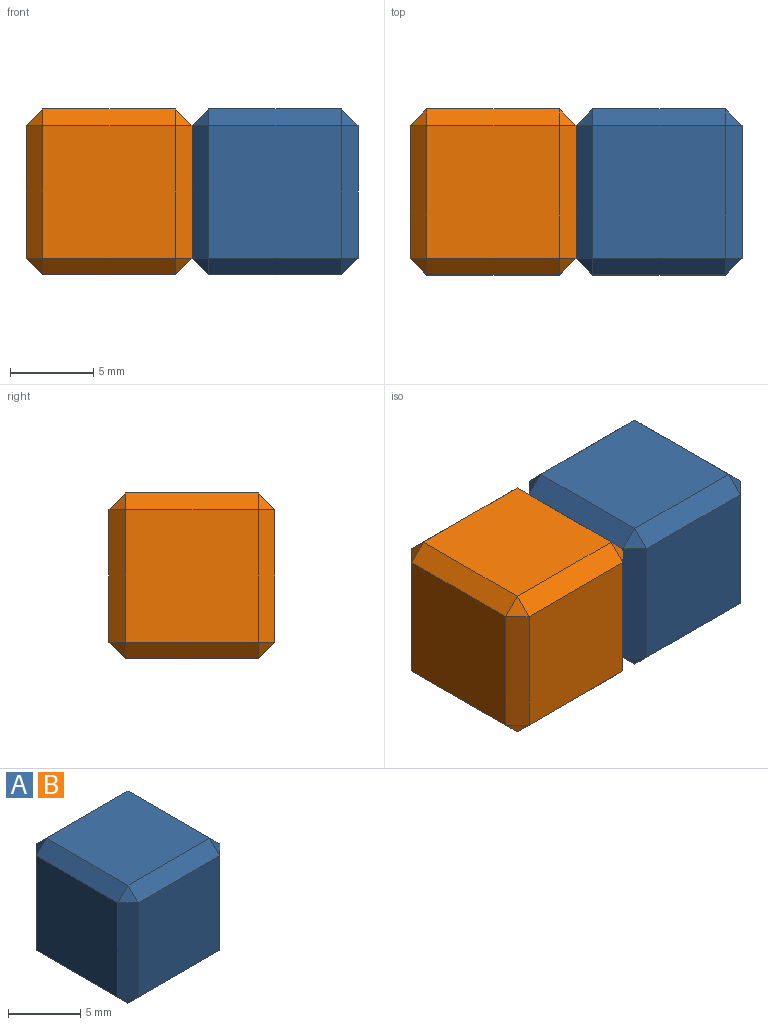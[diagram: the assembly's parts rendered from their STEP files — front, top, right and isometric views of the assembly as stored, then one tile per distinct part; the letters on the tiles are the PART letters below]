
ASSEMBLY  parts=2 mates=1
PART A: 26 faces, bbox 10x10x10 mm
  f0: plane 8x8mm, normal (1,0,0), area 64mm2, adj f11,f20,f21,f25
  f1: plane 8x8mm, normal (0,1,0), area 64mm2, adj f6,f10,f11,f12
  f2: plane 8x8mm, normal (-1,0,0), area 64mm2, adj f6,f9,f13,f14
  f3: plane 8x8mm, normal (0,-1,0), area 64mm2, adj f14,f19,f22,f25
  f4: plane 8x8mm, normal (0,0,1), area 64mm2, adj f9,f10,f19,f20
  f5: plane 8x8mm, normal (0,0,-1), area 64mm2, adj f12,f13,f21,f22
  f6: plane 8x1mm, normal (-0.71,0.71,0), area 11.3mm2, adj f1,f2,f7,f8
  f7: plane 1x1mm, normal (-0.58,0.58,0.58), area 0.9mm2, adj f6,f9,f10
  f8: plane 1x1mm, normal (-0.58,0.58,-0.58), area 0.9mm2, adj f6,f12,f13
  f9: plane 8x1mm, normal (-0.71,0,0.71), area 11.3mm2, adj f2,f4,f7,f15
  f10: plane 8x1mm, normal (0,0.71,0.71), area 11.3mm2, adj f1,f4,f7,f16
  f11: plane 8x1mm, normal (0.71,0.71,0), area 11.3mm2, adj f0,f1,f16,f17
  f12: plane 8x1mm, normal (0,0.71,-0.71), area 11.3mm2, adj f1,f5,f8,f17
  f13: plane 8x1mm, normal (-0.71,0,-0.71), area 11.3mm2, adj f2,f5,f8,f18
  f14: plane 8x1mm, normal (-0.71,-0.71,0), area 11.3mm2, adj f2,f3,f15,f18
  f15: plane 1x1mm, normal (-0.58,-0.58,0.58), area 0.9mm2, adj f9,f14,f19
  f16: plane 1x1mm, normal (0.58,0.58,0.58), area 0.9mm2, adj f10,f11,f20
  f17: plane 1x1mm, normal (0.58,0.58,-0.58), area 0.9mm2, adj f11,f12,f21
  f18: plane 1x1mm, normal (-0.58,-0.58,-0.58), area 0.9mm2, adj f13,f14,f22
  f19: plane 8x1mm, normal (0,-0.71,0.71), area 11.3mm2, adj f3,f4,f15,f23
  f20: plane 8x1mm, normal (0.71,0,0.71), area 11.3mm2, adj f0,f4,f16,f23
  f21: plane 8x1mm, normal (0.71,0,-0.71), area 11.3mm2, adj f0,f5,f17,f24
  f22: plane 8x1mm, normal (0,-0.71,-0.71), area 11.3mm2, adj f3,f5,f18,f24
  f23: plane 1x1mm, normal (0.58,-0.58,0.58), area 0.9mm2, adj f19,f20,f25
  f24: plane 1x1mm, normal (0.58,-0.58,-0.58), area 0.9mm2, adj f21,f22,f25
  f25: plane 8x1mm, normal (0.71,-0.71,0), area 11.3mm2, adj f0,f3,f23,f24
PART B: same geometry as A
PLACE A t=(5.86,5.74,-1.47)mm
PLACE B t=(-4.14,5.74,-1.47)mm
MATE fastened B.f0 <-> A.f2  axis (1,0,0) through (0.86,5.74,3.53)mm
